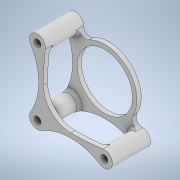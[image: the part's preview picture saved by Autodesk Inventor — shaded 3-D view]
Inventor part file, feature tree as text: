
AUTODESK INVENTOR PART (.ipt)
format: ipt  version: 2020 (Build 240168000, 168)  size: 244,736 bytes
history: native  units: in
note: dims shown in document units (in); Inventor stores cm internally (conversion verified against a paired STEP export)
features: extrude x3, sketch x3, projected_geometry x2, plane x1, fillet x1
ambient origin geometry x8: Origin, YZ Plane, XZ Plane, XY Plane, X Axis, Y Axis, Z Axis, Center Point
bodies: Solid1 (feature_tree)
feature tree (10):
  extrude  "Extrusion1"  Depth=1.8559in
  plane  "Work Plane1"
  extrude  "Extrusion2"  Depth=1.5354in
  extrude  "Extrusion3"  Depth=0.0787in TaperAngle=0.0deg
  fillet  "Fillet1"  [1 undecoded]
  sketch  "Sketch1"  dims[d0=0.1969in d3=1.8559in]
  sketch  "Sketch3"  dims[d5=0.126in d7=1.5354in]
  projected_geometry  "Projected Loop1"
  sketch  "Sketch4"  dims[d8=0.126in d9=1.0591in d10=0.0in d11=-0.1181in d12=0.8228in d13=0.0in d14=0.7441in d15=0.0in d16=0.0787in d17=0.0197in d18=0.0344in d19=0.0197in d20=0.0344in]
  projected_geometry  "Projected Loop2"
note: 1 required parameter value undecoded (feature->parameter linkage not recoverable at this tier; creation-order binding heuristic only, values carry confidence <= 0.55)
